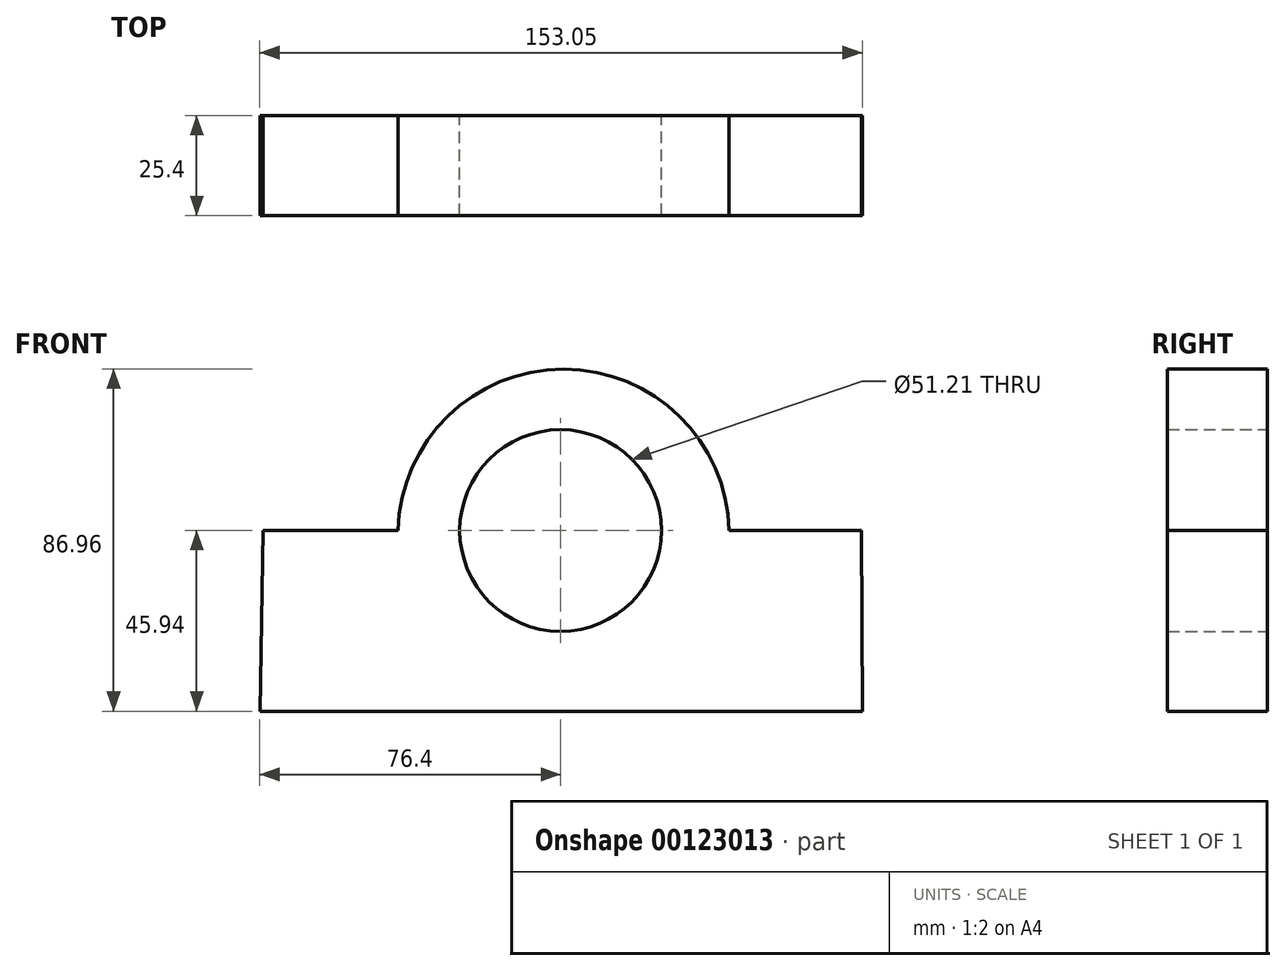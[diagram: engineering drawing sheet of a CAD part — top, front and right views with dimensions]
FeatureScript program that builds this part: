
annotation { "Feature Type Name" : "Feature", "Feature Type Description" : "" }
export const myFeature = defineFeature(function(context is Context, id is Id, definition is map)
    precondition{}
    {
        {
            var Q0;
            Q0=qCreatedBy(makeId("Front.planeOp"),FACE);
            var sketch = newSketch(context, id + "F0", { "sketchPlane" : qUnion([Q0])});
            skCircle(sketch, "E0", {"center": v(0, 0) * mm, "radius": 25.6 * mm});
            skLineSegment(sketch, "E1", {"start": v(-76.4, -45.94) * mm, "end": v(76.65, -45.94) * mm});
            skLineSegment(sketch, "E2", {"start": v(-75.62, 0) * mm, "end": v(-41.3, 0) * mm});
            skLineSegment(sketch, "E3", {"start": v(76.4, 0) * mm, "end": v(42.84, 0) * mm});
            skArc(sketch, "E4", {"start": v(42.84, 0) * mm, "mid": v(0.77, 41.02) * mm, "end": v(-41.3, 0) * mm});
            skLineSegment(sketch, "E5", {"start": v(-75.62, 0) * mm, "end": v(-76.4, -45.94) * mm});
            skLineSegment(sketch, "E6", {"start": v(76.65, -45.94) * mm, "end": v(76.4, 0) * mm});
            skSolve(sketch);
        }
        {
            var Q0;
            Q0 = qSketchRegion(id + "F0", true);
            extrude(context, id + "F1", {"entities" : qUnion([Q0]), "depth" : 25.4 * mm});
        }
    });
